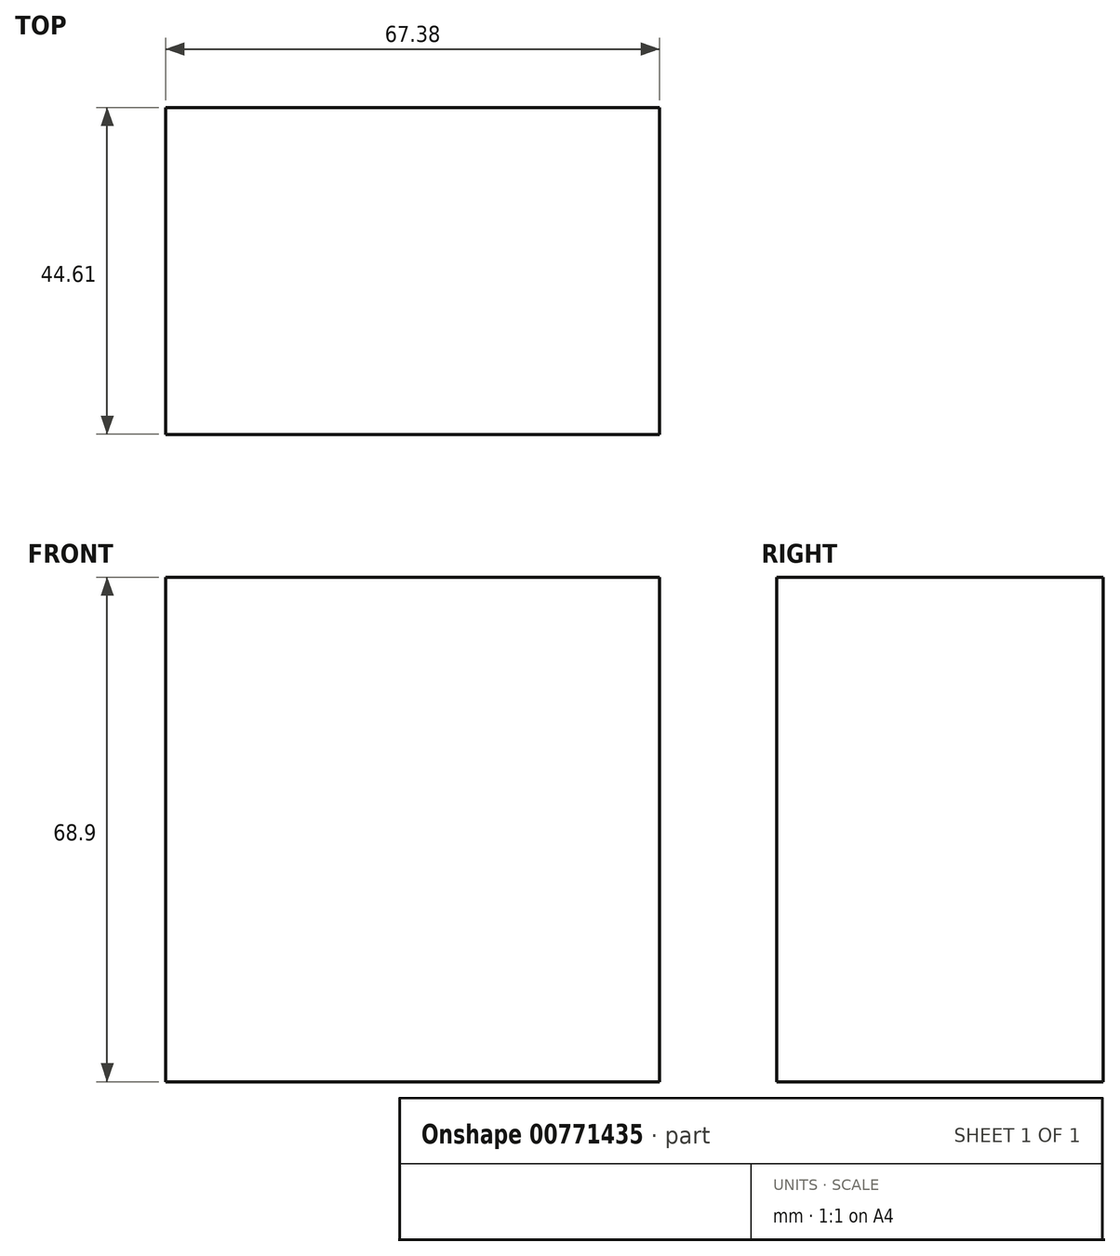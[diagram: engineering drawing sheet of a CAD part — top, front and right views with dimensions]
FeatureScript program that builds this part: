
annotation { "Feature Type Name" : "Feature", "Feature Type Description" : "" }
export const myFeature = defineFeature(function(context is Context, id is Id, definition is map)
    precondition{}
    {
        {
            var Q0;
            Q0=qCreatedBy(makeId("Front.planeOp"),FACE);
            var sketch = newSketch(context, id + "F0", { "sketchPlane" : qUnion([Q0])});
            skLineSegment(sketch, "E0.bottom", {"start": v(33.7, -34.45) * mm, "end": v(-33.7, -34.45) * mm});
            skLineSegment(sketch, "E0.top", {"start": v(33.7, 34.45) * mm, "end": v(-33.7, 34.45) * mm});
            skLineSegment(sketch, "E0.left", {"start": v(33.7, -34.45) * mm, "end": v(33.7, 34.45) * mm});
            skLineSegment(sketch, "E0.right", {"start": v(-33.7, -34.45) * mm, "end": v(-33.7, 34.45) * mm});
            skPoint(sketch, "E0.middle", {"position": v(0, 0) * mm});
            skSolve(sketch);
        }
        {
            var Q0;
            Q0=makeQuery(id+"F0.imprint","IMPRINT",FACE,{"disambiguationData":[TD([[makeQuery(id+"F0.imprint","IMPRINT",EDGE,{"derivedFrom":sQuery(id+"F0.wireOp",EDGE,"E0.bottom")}),-1.0]])]});
            extrude(context, id + "F1", {"entities" : qUnion([Q0]), "depth" : 44.6 * mm, "offsetDistance" : 25 * mm});
        }
    });
